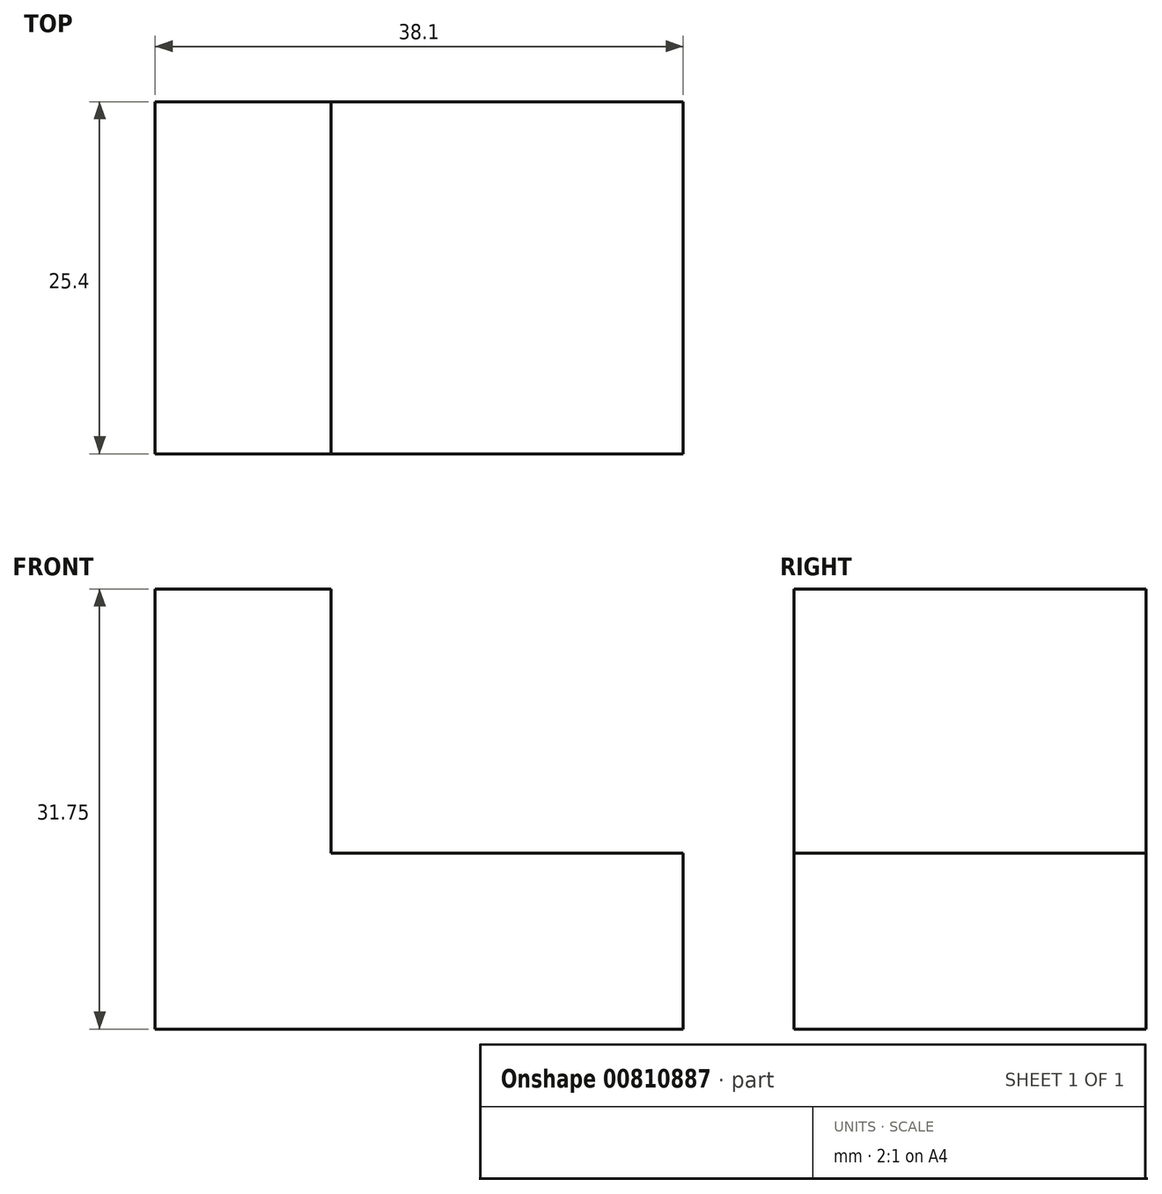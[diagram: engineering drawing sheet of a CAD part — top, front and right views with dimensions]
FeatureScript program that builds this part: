
annotation { "Feature Type Name" : "Feature", "Feature Type Description" : "" }
export const myFeature = defineFeature(function(context is Context, id is Id, definition is map)
    precondition{}
    {
        {
            var Q0;
            Q0=qCreatedBy(makeId("Front.planeOp"),FACE);
            var sketch = newSketch(context, id + "F0", { "sketchPlane" : qUnion([Q0])});
            skLineSegment(sketch, "E0", {"start": v(0, 0) * mm, "end": v(0, 31.75) * mm});
            skLineSegment(sketch, "E1", {"start": v(0, 31.75) * mm, "end": v(12.7, 31.75) * mm});
            skLineSegment(sketch, "E2", {"start": v(12.7, 31.75) * mm, "end": v(12.7, 12.7) * mm});
            skLineSegment(sketch, "E3", {"start": v(12.7, 12.7) * mm, "end": v(38.1, 12.7) * mm});
            skLineSegment(sketch, "E4", {"start": v(38.1, 12.7) * mm, "end": v(38.1, 0) * mm});
            skLineSegment(sketch, "E5", {"start": v(38.1, 0) * mm, "end": v(0, 0) * mm});
            skLineSegment(sketch, "E6", {"start": v(273.94, 128.6) * mm, "end": v(243.86, 119.76) * mm});
            skSolve(sketch);
        }
        {
            var Q0;
            Q0=makeQuery(id+"F0.imprint","IMPRINT",FACE,{"disambiguationData":[TD([[makeQuery(id+"F0.imprint","IMPRINT",EDGE,{"derivedFrom":sQuery(id+"F0.wireOp",EDGE,"E0")}),-1.0]])]});
            extrude(context, id + "F1", {"entities" : qUnion([Q0]), "depth" : 25.4 * mm, "offsetDistance" : 25.4 * mm});
        }
    });
